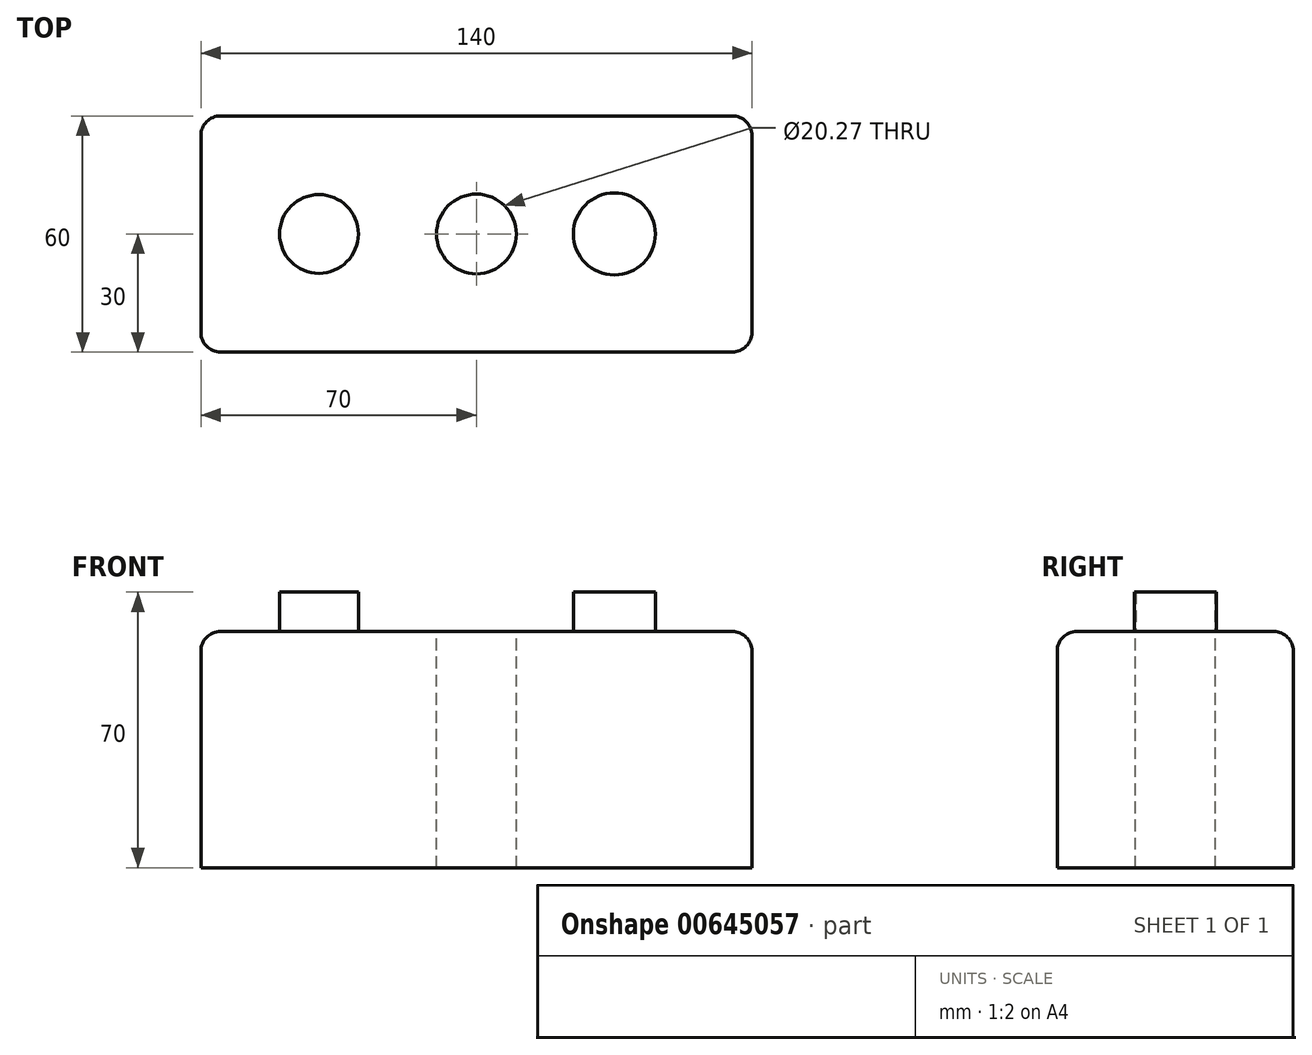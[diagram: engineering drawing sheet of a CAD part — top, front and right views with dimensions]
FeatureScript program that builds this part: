
annotation { "Feature Type Name" : "Feature", "Feature Type Description" : "" }
export const myFeature = defineFeature(function(context is Context, id is Id, definition is map)
    precondition{}
    {
        {
            var Q0;
            Q0=qCreatedBy(makeId("Top.planeOp"),FACE);
            var sketch = newSketch(context, id + "F0", { "sketchPlane" : qUnion([Q0])});
            skLineSegment(sketch, "E0.bottom", {"start": v(70, -30) * mm, "end": v(-70, -30) * mm});
            skLineSegment(sketch, "E0.top", {"start": v(70, 30) * mm, "end": v(-70, 30) * mm});
            skLineSegment(sketch, "E0.left", {"start": v(70, -30) * mm, "end": v(70, 30) * mm});
            skLineSegment(sketch, "E0.right", {"start": v(-70, -30) * mm, "end": v(-70, 30) * mm});
            skPoint(sketch, "E0.middle", {"position": v(0, 0) * mm});
            skSolve(sketch);
        }
        {
            var Q0;
            Q0=makeQuery(id+"F0.imprint","IMPRINT",FACE,{"disambiguationData":[TD([[makeQuery(id+"F0.imprint","IMPRINT",EDGE,{"derivedFrom":sQuery(id+"F0.wireOp",EDGE,"E0.bottom")}),-1.0]])]});
            extrude(context, id + "F1", {"entities" : qUnion([Q0]), "depth" : 60 * mm, "offsetDistance" : 25 * mm});
        }
        {
            var Q0;
            Q0=makeQuery(id+"F1.opExtrude","CAP_FACE",FACE,{"disambiguationData":[OSD([sQuery(id+"F0.wireOp",EDGE,"E0.bottom"),sQuery(id+"F0.wireOp",EDGE,"E0.top"),sQuery(id+"F0.wireOp",EDGE,"E0.left"),sQuery(id+"F0.wireOp",EDGE,"E0.right")])],"isStart":false});
            var sketch = newSketch(context, id + "F2", { "sketchPlane" : qUnion([Q0])});
            skCircle(sketch, "E1", {"center": v(-40, 0) * mm, "radius": 10 * mm});
            skSolve(sketch);
        }
        {
            var Q0;
            Q0=makeQuery(id+"F2.imprint","IMPRINT",FACE,{"disambiguationData":[TD([[makeQuery(id+"F2.imprint","IMPRINT",EDGE,{"derivedFrom":sQuery(id+"F2.wireOp",EDGE,"E1")}),-1.0]])]});
            var sketch = newSketch(context, id + "F3", { "sketchPlane" : qUnion([Q0])});
            skCircle(sketch, "E2", {"center": v(35.04, 0) * mm, "radius": 10.42 * mm});
            skSolve(sketch);
        }
        {
            var Q0;
            Q0=makeQuery(id+"F2.imprint","IMPRINT",FACE,{"disambiguationData":[TD([[makeQuery(id+"F2.imprint","IMPRINT",EDGE,{"derivedFrom":sQuery(id+"F2.wireOp",EDGE,"E1")}),-1.0]])]});
            var sketch = newSketch(context, id + "F4", { "sketchPlane" : qUnion([Q0])});
            skCircle(sketch, "E3", {"center": v(0, 0) * mm, "radius": 10.13 * mm});
            skSolve(sketch);
        }
        {
            var Q0;
            Q0=makeQuery(id+"F2.imprint","IMPRINT",FACE,{"disambiguationData":[TD([[makeQuery(id+"F2.imprint","IMPRINT",EDGE,{"derivedFrom":sQuery(id+"F2.wireOp",EDGE,"E1")}),1.0]])]});
            extrude(context, id + "F5", {"entities" : qUnion([Q0]), "operationType" : NewBodyOperationType.ADD, "depth" : 10 * mm, "offsetDistance" : 25 * mm});
        }
        {
            var Q0;
            Q0 = qSketchRegion(id + "F4", true);
            extrude(context, id + "F6", {"entities" : qUnion([Q0]), "operationType" : NewBodyOperationType.REMOVE, "oppositeDirection" : true, "depth" : 175 * mm, "offsetDistance" : 25 * mm});
        }
        {
            var Q0;
            Q0=makeQuery(id+"F3.imprint","IMPRINT",FACE,{"disambiguationData":[TD([[makeQuery(id+"F3.imprint","IMPRINT",EDGE,{"derivedFrom":sQuery(id+"F3.wireOp",EDGE,"E2")}),1.0]])]});
            extrude(context, id + "F7", {"entities" : qUnion([Q0]), "operationType" : NewBodyOperationType.ADD, "depth" : 10 * mm, "offsetDistance" : 25 * mm});
        }
        {
            var Q0;
            Q0=makeQuery(id+"F1.opExtrude","CAP_EDGE",EDGE,{"disambiguationData":[OSD([sQuery(id+"F0.wireOp",EDGE,"E0.top")])],"isStart":false});
            var Q1;
            Q1=makeQuery(id+"F1.opExtrude","CAP_EDGE",EDGE,{"disambiguationData":[OSD([sQuery(id+"F0.wireOp",EDGE,"E0.left")])],"isStart":false});
            var Q2;
            Q2=makeQuery(id+"F1.opExtrude","CAP_EDGE",EDGE,{"disambiguationData":[OSD([sQuery(id+"F0.wireOp",EDGE,"E0.bottom")])],"isStart":false});
            var Q3;
            Q3=makeQuery(id+"F1.opExtrude","CAP_EDGE",EDGE,{"disambiguationData":[OSD([sQuery(id+"F0.wireOp",EDGE,"E0.right")])],"isStart":false});
            var Q4;
            Q4=makeQuery(id+"F1.opExtrude","SWEPT_EDGE",EDGE,{"disambiguationData":[OSD([sQuery(id+"F0.wireOp",EDGE,"E0.top"),sQuery(id+"F0.wireOp",EDGE,"E0.right")])]});
            var Q5;
            Q5=makeQuery(id+"F1.opExtrude","SWEPT_EDGE",EDGE,{"disambiguationData":[OSD([sQuery(id+"F0.wireOp",EDGE,"E0.bottom"),sQuery(id+"F0.wireOp",EDGE,"E0.right")])]});
            var Q6;
            Q6=makeQuery(id+"F1.opExtrude","SWEPT_EDGE",EDGE,{"disambiguationData":[OSD([sQuery(id+"F0.wireOp",EDGE,"E0.bottom"),sQuery(id+"F0.wireOp",EDGE,"E0.left")])]});
            var Q7;
            Q7=makeQuery(id+"F1.opExtrude","SWEPT_EDGE",EDGE,{"disambiguationData":[OSD([sQuery(id+"F0.wireOp",EDGE,"E0.top"),sQuery(id+"F0.wireOp",EDGE,"E0.left")])]});
            fillet(context, id + "F8", {"entities" : qUnion([Q0, Q1, Q2, Q3, Q4, Q5, Q6, Q7]), "radius" : 5 * mm, "tangentPropagation" : true, "allowEdgeOverflow" : false});
        }
    });
